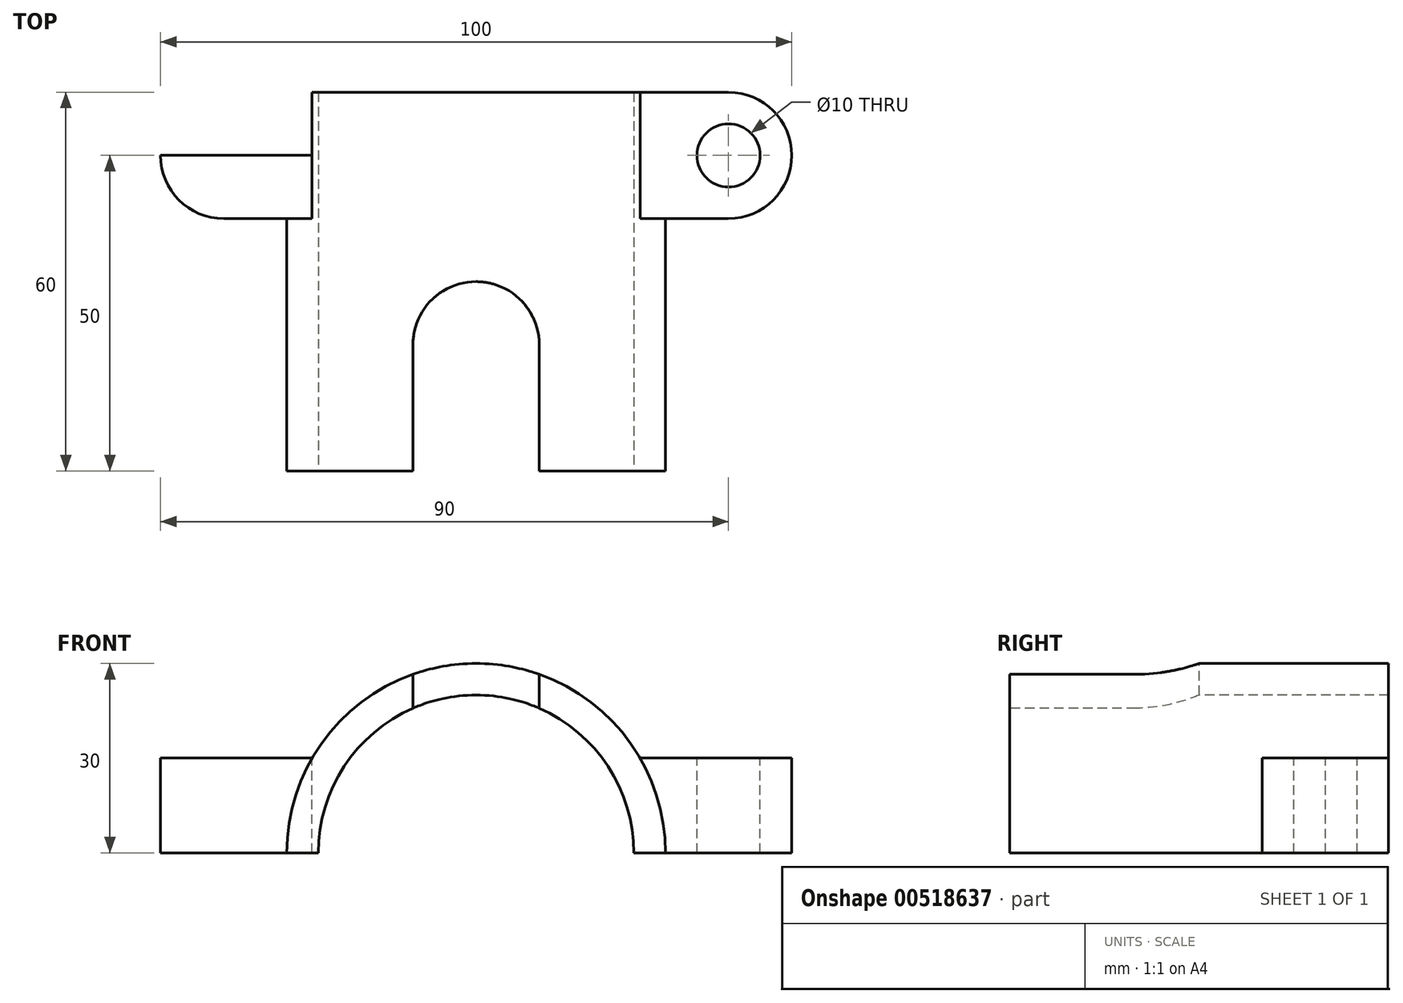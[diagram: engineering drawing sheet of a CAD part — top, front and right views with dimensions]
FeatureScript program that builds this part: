
annotation { "Feature Type Name" : "Feature", "Feature Type Description" : "" }
export const myFeature = defineFeature(function(context is Context, id is Id, definition is map)
    precondition{}
    {
        {
            var Q0;
            Q0=qCreatedBy(makeId("Front.planeOp"),FACE);
            var sketch = newSketch(context, id + "F0", { "sketchPlane" : qUnion([Q0])});
            skCircle(sketch, "E0", {"center": v(0, 0) * mm, "radius": 30 * mm});
            skLineSegment(sketch, "E1", {"start": v(-30, 0) * mm, "end": v(30, 0) * mm});
            skSolve(sketch);
        }
        {
            var Q0;
            {var subQ0=sQuery(id+"F0.wireOp",EDGE,"E1");Q0=makeQuery(id+"F0.imprint","IMPRINT",FACE,{"disambiguationData":[TD([[makeQuery(id+"F0.imprint","IMPRINT",EDGE,{"derivedFrom":subQ0}),1.0]])]});}
            extrude(context, id + "F1", {"entities" : qUnion([Q0]), "depth" : 60 * mm, "offsetDistance" : 25 * mm});
        }
        {
            var Q0;
            Q0=makeQuery(id+"F1.opExtrude","SWEPT_FACE",FACE,{"disambiguationData":[OSD([sQuery(id+"F0.wireOp",EDGE,"E1")])]});
            var sketch = newSketch(context, id + "F2", { "sketchPlane" : qUnion([Q0])});
            skLineSegment(sketch, "E2", {"start": v(-40, 10) * mm, "end": v(40, 10) * mm, "construction": true});
            skArc(sketch, "E3.0.startCap", {"start": v(-40, 0) * mm, "mid": v(-50, 10) * mm, "end": v(-40, 20) * mm});
            skArc(sketch, "E3.0.endCap", {"start": v(40, 20) * mm, "mid": v(50, 10) * mm, "end": v(40, 0) * mm});
            skLineSegment(sketch, "E3.0.left", {"start": v(-40, 20) * mm, "end": v(40, 20) * mm});
            skLineSegment(sketch, "E3.0.right", {"start": v(-40, 0) * mm, "end": v(40, 0) * mm});
            skSolve(sketch);
        }
        {
            var Q0;
            Q0=qSketchRegion(id+"F2",true);
            extrude(context, id + "F3", {"entities" : qUnion([Q0]), "operationType" : NewBodyOperationType.ADD, "oppositeDirection" : true, "depth" : 15 * mm, "offsetDistance" : 25 * mm});
        }
        {
            var Q0;
            {var subQ0=sQuery(id+"F2.wireOp",EDGE,"E3.0.left");var subQ1=sQuery(id+"F2.wireOp",EDGE,"E3.0.startCap");var subQ3=sQuery(id+"F2.wireOp",EDGE,"E3.0.right");Q0=makeQuery(id+"F3.boolean.opBoolean","SPLIT",FACE,{"disambiguationData":[TD([makeQuery(id+"F3.opExtrude","SWEPT_FACE",FACE,{"disambiguationData":[OSD([subQ1])]})])],"derivedFrom":makeQuery(id+"F3.opExtrude","CAP_FACE",FACE,{"disambiguationData":[OSD([subQ1,sQuery(id+"F2.wireOp",EDGE,"E3.0.endCap"),subQ0,subQ3])],"isStart":false})});}
            var sketch = newSketch(context, id + "F4", { "sketchPlane" : qUnion([Q0])});
            skLineSegment(sketch, "E4", {"start": v(-40, -20) * mm, "end": v(-40, 5.06) * mm});
            skLineSegment(sketch, "E5", {"start": v(-25.98, -10) * mm, "end": v(-53.03, -10) * mm});
            skPoint(sketch, "E5.endSnap0", {"position": v(-25.98, -10) * mm});
            skCircle(sketch, "E6", {"center": v(-40, -10) * mm, "radius": 5 * mm});
            skSolve(sketch);
        }
        {
            var Q0;
            {var subQ0=sQuery(id+"F4.wireOp",EDGE,"E5");var subQ1=sQuery(id+"F4.wireOp",EDGE,"E4");var subQ2=makeQuery(id+"F4.imprint","INTERSECT",VERTEX,{"derivedFrom":[subQ1,subQ0]});Q0=makeQuery(id+"F4.imprint","IMPRINT",FACE,{"disambiguationData":[TD([[makeQuery(id+"F4.imprint","IMPRINT",EDGE,{"disambiguationData":[TD([[subQ2,-1.0]])],"derivedFrom":subQ1}),1.0]])]});}
            var Q1;
            {var subQ0=sQuery(id+"F4.wireOp",EDGE,"E5");var subQ1=sQuery(id+"F4.wireOp",EDGE,"E4");var subQ2=makeQuery(id+"F4.imprint","INTERSECT",VERTEX,{"derivedFrom":[subQ1,subQ0]});Q1=makeQuery(id+"F4.imprint","IMPRINT",FACE,{"disambiguationData":[TD([[makeQuery(id+"F4.imprint","IMPRINT",EDGE,{"disambiguationData":[TD([[subQ2,-1.0]])],"derivedFrom":subQ1}),-1.0]])]});}
            var Q2;
            {var subQ0=sQuery(id+"F4.wireOp",EDGE,"E6");var subQ1=sQuery(id+"F4.wireOp",EDGE,"E4");var subQ2=makeQuery(id+"F4.imprint","INTERSECT",VERTEX,{"disambiguationData":[OD(0.0)],"derivedFrom":[subQ1,subQ0]});Q2=makeQuery(id+"F4.imprint","IMPRINT",FACE,{"disambiguationData":[TD([[makeQuery(id+"F4.imprint","IMPRINT",EDGE,{"disambiguationData":[TD([[subQ2,-1.0]])],"derivedFrom":subQ1}),-1.0]])]});}
            var Q3;
            {var subQ0=sQuery(id+"F4.wireOp",EDGE,"E6");var subQ1=sQuery(id+"F4.wireOp",EDGE,"E4");var subQ2=makeQuery(id+"F4.imprint","INTERSECT",VERTEX,{"disambiguationData":[OD(0.0)],"derivedFrom":[subQ1,subQ0]});Q3=makeQuery(id+"F4.imprint","IMPRINT",FACE,{"disambiguationData":[TD([[makeQuery(id+"F4.imprint","IMPRINT",EDGE,{"disambiguationData":[TD([[subQ2,-1.0]])],"derivedFrom":subQ1}),1.0]])]});}
            var Q4;
            Q4=sQuery(id+"F4.wireOp",EDGE,"E6");
            extrude(context, id + "F5", {"entities" : qUnion([Q0, Q1, Q2, Q3]), "operationType" : NewBodyOperationType.REMOVE, "surfaceEntities" : qUnion([Q4]), "endBound" : BoundingType.THROUGH_ALL, "oppositeDirection" : true, "depth" : 25 * mm, "offsetDistance" : 25 * mm});
        }
        {
            var Q0;
            {var subQ0=sQuery(id+"F2.wireOp",EDGE,"E3.0.left");var subQ1=sQuery(id+"F2.wireOp",EDGE,"E3.0.endCap");var subQ3=sQuery(id+"F2.wireOp",EDGE,"E3.0.right");Q0=makeQuery(id+"F3.boolean.opBoolean","SPLIT",FACE,{"disambiguationData":[TD([makeQuery(id+"F3.opExtrude","SWEPT_FACE",FACE,{"disambiguationData":[OSD([subQ1])]})])],"derivedFrom":makeQuery(id+"F3.opExtrude","CAP_FACE",FACE,{"disambiguationData":[OSD([sQuery(id+"F2.wireOp",EDGE,"E3.0.startCap"),subQ1,subQ0,subQ3])],"isStart":false})});}
            var sketch = newSketch(context, id + "F6", { "sketchPlane" : qUnion([Q0])});
            skLineSegment(sketch, "E7", {"start": v(25.98, -10) * mm, "end": v(51.34, -10) * mm});
            skLineSegment(sketch, "E8", {"start": v(40, 0) * mm, "end": v(40, -31.13) * mm});
            skCircle(sketch, "E9", {"center": v(40, -10) * mm, "radius": 5 * mm});
            skSolve(sketch);
        }
        {
            var Q0;
            {var subQ0=sQuery(id+"F6.wireOp",EDGE,"E9");var subQ1=sQuery(id+"F6.wireOp",EDGE,"E7");var subQ2=makeQuery(id+"F6.imprint","INTERSECT",VERTEX,{"disambiguationData":[OD(0.0)],"derivedFrom":[subQ1,subQ0]});Q0=makeQuery(id+"F6.imprint","IMPRINT",FACE,{"disambiguationData":[TD([[makeQuery(id+"F6.imprint","IMPRINT",EDGE,{"disambiguationData":[TD([[subQ2,-1.0]])],"derivedFrom":subQ1}),1.0]])]});}
            var Q1;
            {var subQ0=sQuery(id+"F6.wireOp",EDGE,"E8");var subQ1=sQuery(id+"F6.wireOp",EDGE,"E7");var subQ2=makeQuery(id+"F6.imprint","INTERSECT",VERTEX,{"derivedFrom":[subQ1,subQ0]});Q1=makeQuery(id+"F6.imprint","IMPRINT",FACE,{"disambiguationData":[TD([[makeQuery(id+"F6.imprint","IMPRINT",EDGE,{"disambiguationData":[TD([[subQ2,-1.0]])],"derivedFrom":subQ1}),1.0]])]});}
            var Q2;
            {var subQ0=sQuery(id+"F6.wireOp",EDGE,"E8");var subQ1=sQuery(id+"F6.wireOp",EDGE,"E7");var subQ2=makeQuery(id+"F6.imprint","INTERSECT",VERTEX,{"derivedFrom":[subQ1,subQ0]});Q2=makeQuery(id+"F6.imprint","IMPRINT",FACE,{"disambiguationData":[TD([[makeQuery(id+"F6.imprint","IMPRINT",EDGE,{"disambiguationData":[TD([[subQ2,-1.0]])],"derivedFrom":subQ1}),-1.0]])]});}
            var Q3;
            {var subQ0=sQuery(id+"F6.wireOp",EDGE,"E9");var subQ1=sQuery(id+"F6.wireOp",EDGE,"E7");var subQ2=makeQuery(id+"F6.imprint","INTERSECT",VERTEX,{"disambiguationData":[OD(0.0)],"derivedFrom":[subQ1,subQ0]});Q3=makeQuery(id+"F6.imprint","IMPRINT",FACE,{"disambiguationData":[TD([[makeQuery(id+"F6.imprint","IMPRINT",EDGE,{"disambiguationData":[TD([[subQ2,-1.0]])],"derivedFrom":subQ1}),-1.0]])]});}
            var Q4;
            Q4=sQuery(id+"F6.wireOp",EDGE,"E9");
            extrude(context, id + "F7", {"entities" : qUnion([Q0, Q1, Q2, Q3]), "operationType" : NewBodyOperationType.REMOVE, "surfaceEntities" : qUnion([Q4]), "endBound" : BoundingType.THROUGH_ALL, "oppositeDirection" : true, "depth" : 25 * mm, "offsetDistance" : 25 * mm});
        }
        {
            var Q0;
            Q0=makeQuery(id+"F1.opExtrude","CAP_FACE",FACE,{"disambiguationData":[OSD([sQuery(id+"F0.wireOp",EDGE,"E0"),sQuery(id+"F0.wireOp",EDGE,"E1")])],"isStart":false});
            var sketch = newSketch(context, id + "F8", { "sketchPlane" : qUnion([Q0])});
            skCircle(sketch, "E10", {"center": v(0, 0) * mm, "radius": 25 * mm});
            skSolve(sketch);
        }
        {
            var Q0;
            {var subQ0=sQuery(id+"F8.wireOp",EDGE,"E10");var subQ1=makeQuery(id+"F1.opExtrude","CAP_EDGE",EDGE,{"disambiguationData":[OSD([sQuery(id+"F0.wireOp",EDGE,"E1")])],"isStart":false});var subQ2=makeQuery(id+"F8.imprint","INTERSECT",VERTEX,{"disambiguationData":[OD(0.0)],"derivedFrom":[subQ1,subQ0]});Q0=makeQuery(id+"F8.imprint","IMPRINT",FACE,{"disambiguationData":[TD([[makeQuery(id+"F8.imprint","IMPRINT",EDGE,{"disambiguationData":[TD([[subQ2,1.0]])],"derivedFrom":subQ0}),1.0]])]});}
            extrude(context, id + "F9", {"entities" : qUnion([Q0]), "operationType" : NewBodyOperationType.REMOVE, "endBound" : BoundingType.THROUGH_ALL, "oppositeDirection" : true, "depth" : 25 * mm, "offsetDistance" : 25 * mm});
        }
        {
            var Q0;
            Q0=qCreatedBy(makeId("Top.planeOp"),FACE);
            var sketch = newSketch(context, id + "F10", { "sketchPlane" : qUnion([Q0])});
            skLineSegment(sketch, "E11", {"start": v(0, -60) * mm, "end": v(10, -60) * mm});
            skLineSegment(sketch, "E12", {"start": v(0, -60) * mm, "end": v(-10, -60) * mm});
            skLineSegment(sketch, "E13", {"start": v(-10, -60) * mm, "end": v(-10, -30) * mm});
            skLineSegment(sketch, "E14", {"start": v(-10, -30) * mm, "end": v(10, -30) * mm});
            skLineSegment(sketch, "E15", {"start": v(10, -30) * mm, "end": v(10, -60) * mm});
            skSolve(sketch);
        }
        {
            var Q0;
            Q0=makeQuery(id+"F10.imprint","IMPRINT",FACE,{"disambiguationData":[TD([[makeQuery(id+"F10.imprint","IMPRINT",EDGE,{"derivedFrom":sQuery(id+"F10.wireOp",EDGE,"E11")}),1.0]])]});
            var Q1;
            Q1=makeQuery(id+"F1.opExtrude","SWEPT_FACE",FACE,{"disambiguationData":[OSD([sQuery(id+"F0.wireOp",EDGE,"E0")])]});
            extrude(context, id + "F11", {"entities" : qUnion([Q0]), "operationType" : NewBodyOperationType.REMOVE, "endBound" : BoundingType.UP_TO_SURFACE, "depth" : 25 * mm, "endBoundEntityFace" : qUnion([Q1]), "offsetDistance" : 25 * mm});
        }
        {
            var Q0;
            Q0=makeQuery(id+"F11.boolean.opBoolean","COPY",EDGE,{"derivedFrom":makeQuery(id+"F11.opExtrude","SWEPT_EDGE",EDGE,{"disambiguationData":[OSD([sQuery(id+"F10.wireOp",EDGE,"E13"),sQuery(id+"F10.wireOp",EDGE,"E14")])]})});
            var Q1;
            Q1=makeQuery(id+"F11.boolean.opBoolean","COPY",EDGE,{"derivedFrom":makeQuery(id+"F11.opExtrude","SWEPT_EDGE",EDGE,{"disambiguationData":[OSD([sQuery(id+"F10.wireOp",EDGE,"E14"),sQuery(id+"F10.wireOp",EDGE,"E15")])]})});
            fillet(context, id + "F12", {"entities" : qUnion([Q0, Q1]), "radius" : 10 * mm, "tangentPropagation" : true, "allowEdgeOverflow" : false});
        }
    });
